# Revit family: 2054910 Accessories_Sylvania_MC II-Trimless-End Cap
name_source: partatom
category: Generic Models
revit_build: Autodesk Revit 2015 (Build: 20140606_1530(x64)
units: mm (PartAtom-declared; Revit-internal decimal feet)

## types (1)
- MC2 TRIMLESS END CAP WHT
    Catalog Number = 2054910 MC2 TRIMLESS END CAP WHT
    Default Elevation = 0 mm  [stored 0 ft]
    Description = Mini Continuum II Trimlees End Cap
    End Cap = Metal_Sylvania_Mini Continuum II_White
    Height = 86 mm  [stored 0.282152 ft]
    Manufacturer = Feilo Sylvania
    Model = MC2 TRIMLESS END CAP WHT
    Product Family = Mini Continuum II-Direct-Trimless-Accessories
    Product Page URL = http://www.feilosylvania.com
    URL = http://www.feilosylvania.com
    Weight = 0.50 kg
    Width = 54 mm  [stored 0.177165 ft]

note: [stored X ft] marks values corroborated as IEEE doubles in the binary element streams (Revit-internal decimal feet)

## geometry (parser evidence)
native form markers: Sweep x3
no freeform markers — native parametric forms only
